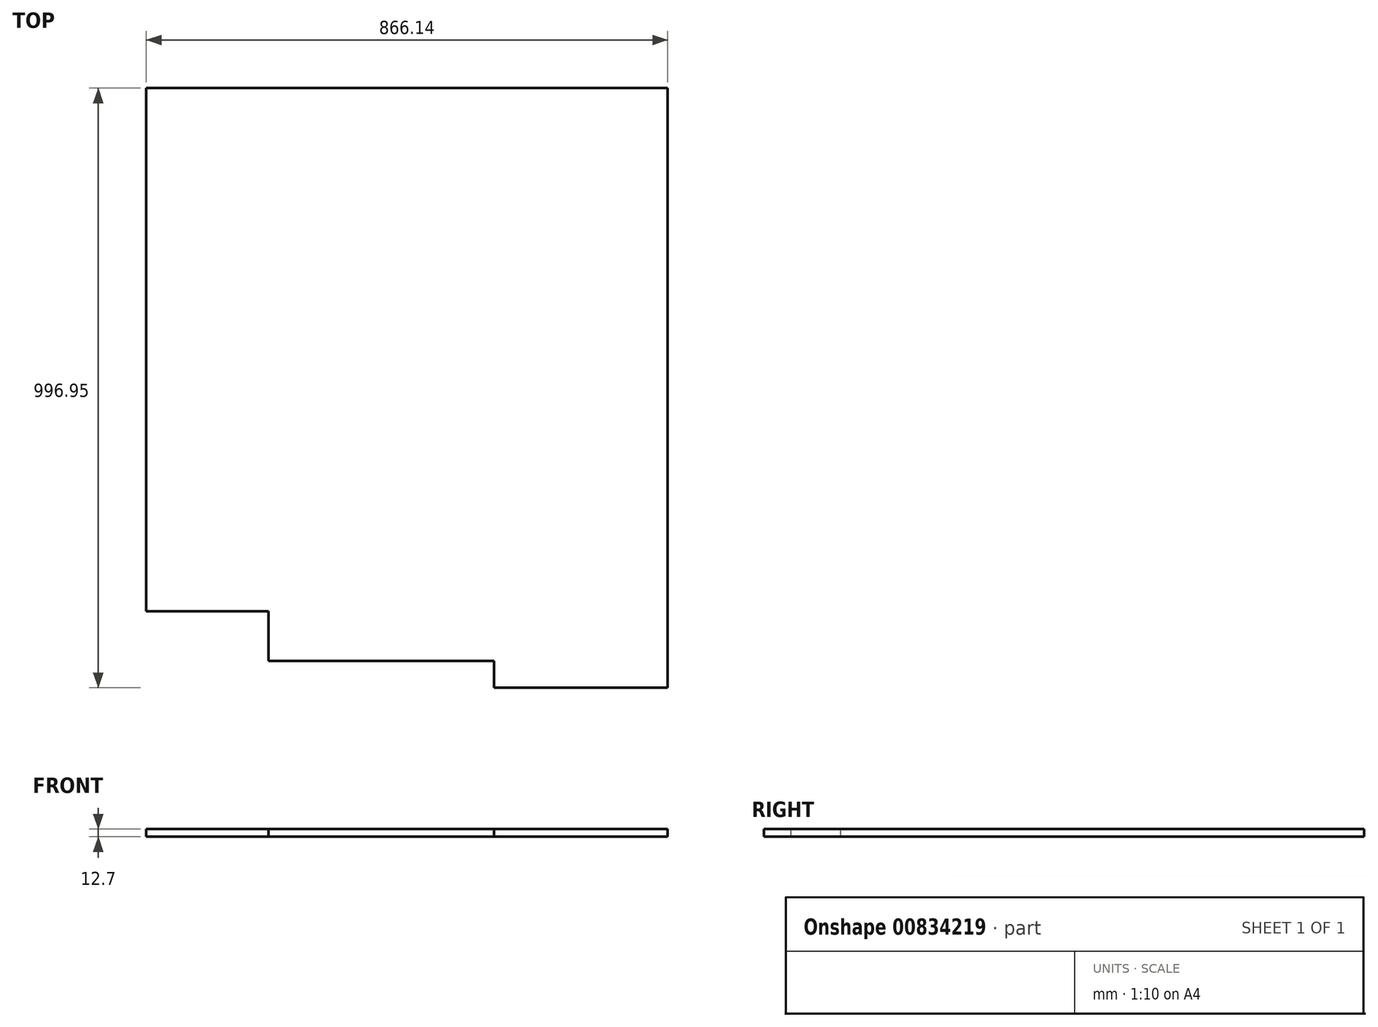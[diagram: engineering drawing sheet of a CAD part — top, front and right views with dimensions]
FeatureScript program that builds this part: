
annotation { "Feature Type Name" : "Feature", "Feature Type Description" : "" }
export const myFeature = defineFeature(function(context is Context, id is Id, definition is map)
    precondition{}
    {
        {
            var Q0;
            Q0=qCreatedBy(makeId("Top.planeOp"),FACE);
            var sketch = newSketch(context, id + "F0", { "sketchPlane" : qUnion([Q0])});
            skPoint(sketch, "E0", {"position": v(-393.43, 496.15) * mm});
            skLineSegment(sketch, "E1", {"start": v(-393.43, 496.15) * mm, "end": v(472.7, 496.15) * mm});
            skLineSegment(sketch, "E2", {"start": v(115.84, 477.1) * mm, "end": v(123.46, 477.1) * mm});
            skLineSegment(sketch, "E3", {"start": v(-393.43, 496.15) * mm, "end": v(-393.43, 153.25) * mm});
            skLineSegment(sketch, "E4", {"start": v(-393.43, 153.25) * mm, "end": v(-393.43, -373.8) * mm});
            skLineSegment(sketch, "E5", {"start": v(-190.23, -176.95) * mm, "end": v(-190.23, -169.33) * mm});
            skLineSegment(sketch, "E6", {"start": v(184.42, -151.55) * mm, "end": v(203.47, -151.55) * mm});
            skLineSegment(sketch, "E7", {"start": v(472.7, 496.15) * mm, "end": v(472.7, -170.6) * mm});
            skPoint(sketch, "E8", {"position": v(-171.18, -373.8) * mm});
            skLineSegment(sketch, "E9", {"start": v(-393.43, -373.8) * mm, "end": v(-190.23, -373.8) * mm});
            skLineSegment(sketch, "E10", {"start": v(-190.23, -373.8) * mm, "end": v(-190.23, -456.35) * mm});
            skLineSegment(sketch, "E11", {"start": v(-190.23, -456.35) * mm, "end": v(184.42, -456.35) * mm});
            skLineSegment(sketch, "E12", {"start": v(184.42, -456.35) * mm, "end": v(184.42, -500.8) * mm});
            skLineSegment(sketch, "E13", {"start": v(184.42, -500.8) * mm, "end": v(472.7, -500.8) * mm});
            skLineSegment(sketch, "E14", {"start": v(472.7, -170.6) * mm, "end": v(472.7, -500.8) * mm});
            skPoint(sketch, "E15.right.start.orphan", {"position": v(-44.18, 477.1) * mm});
            skSolve(sketch);
        }
        {
            var Q0;
            Q0=makeQuery(id+"F0.imprint","IMPRINT",FACE,{"disambiguationData":[TD([[makeQuery(id+"F0.imprint","IMPRINT",EDGE,{"derivedFrom":sQuery(id+"F0.wireOp",EDGE,"E1")}),-1.0]])]});
            extrude(context, id + "F1", {"entities" : qUnion([Q0]), "depth" : 12.7 * mm, "offsetDistance" : 25.4 * mm});
        }
    });
